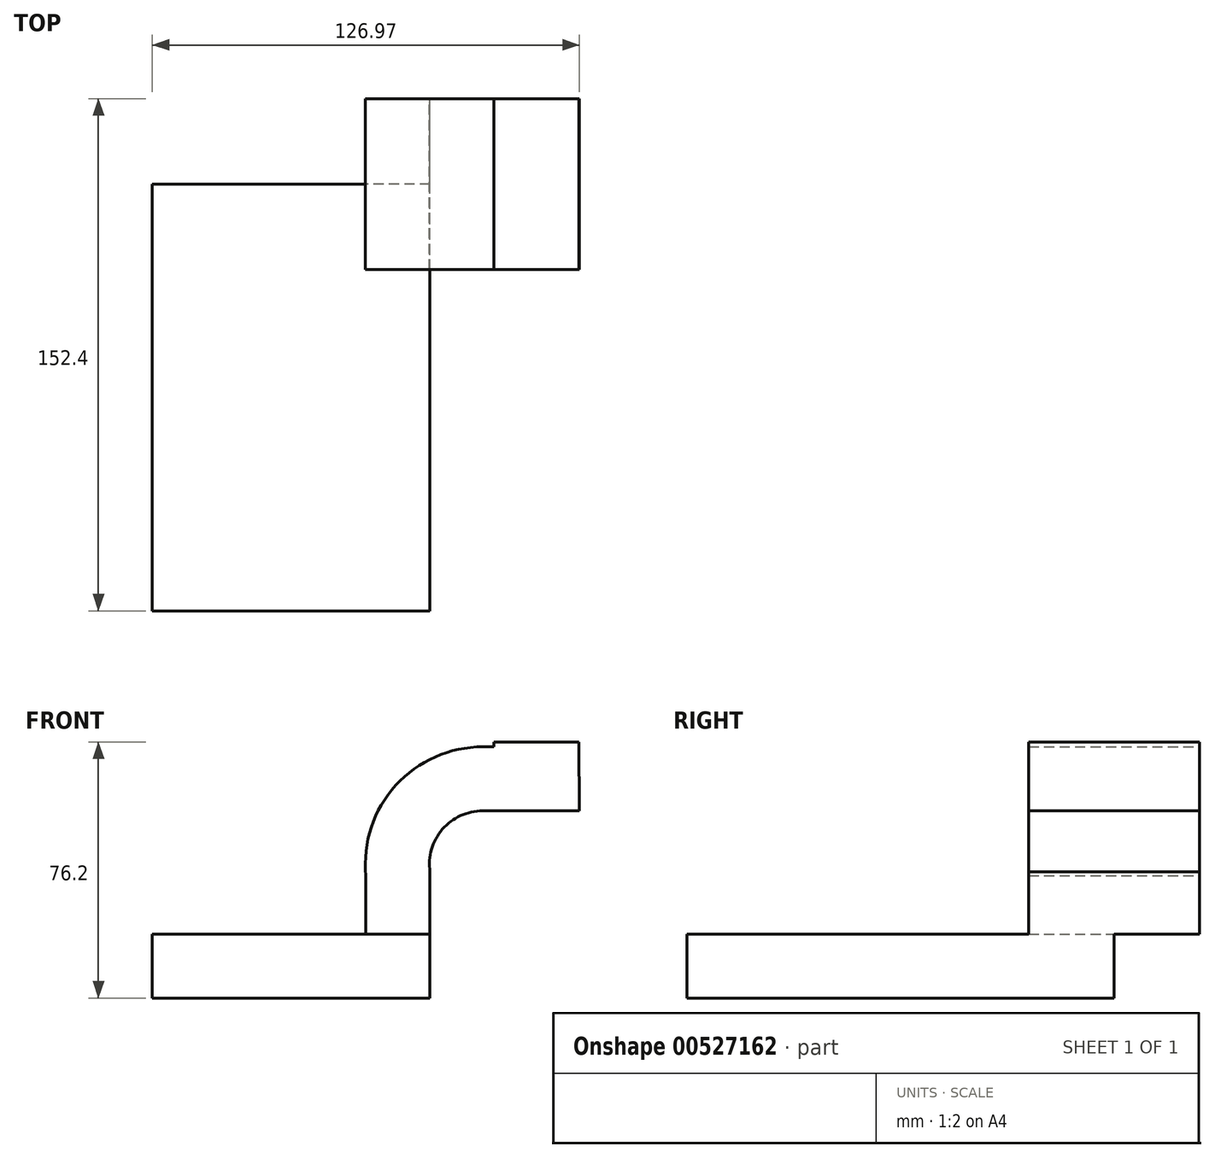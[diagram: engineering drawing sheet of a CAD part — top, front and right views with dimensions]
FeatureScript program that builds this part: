
annotation { "Feature Type Name" : "Feature", "Feature Type Description" : "" }
export const myFeature = defineFeature(function(context is Context, id is Id, definition is map)
    precondition{}
    {
        {
            var Q0;
            Q0=qCreatedBy(makeId("Front.planeOp"),FACE);
            var sketch = newSketch(context, id + "F0", { "sketchPlane" : qUnion([Q0])});
            skLineSegment(sketch, "E0.bottom", {"start": v(41.27, 9.53) * mm, "end": v(-41.28, 9.53) * mm});
            skLineSegment(sketch, "E0.top", {"start": v(41.28, -9.52) * mm, "end": v(-41.27, -9.52) * mm});
            skLineSegment(sketch, "E0.left", {"start": v(41.27, 9.53) * mm, "end": v(41.28, -9.52) * mm});
            skLineSegment(sketch, "E0.right", {"start": v(-41.28, 9.53) * mm, "end": v(-41.27, -9.52) * mm});
            skPoint(sketch, "E0.middle", {"position": v(0, 0) * mm});
            skLineSegment(sketch, "E1.bottom", {"start": v(60.33, 66.68) * mm, "end": v(111.13, 66.68) * mm});
            skLineSegment(sketch, "E1.top", {"start": v(60.33, 38.1) * mm, "end": v(111.13, 38.1) * mm});
            skLineSegment(sketch, "E1.left", {"start": v(60.33, 66.68) * mm, "end": v(60.33, 38.1) * mm});
            skLineSegment(sketch, "E1.right", {"start": v(111.13, 66.68) * mm, "end": v(111.13, 38.1) * mm});
            skPoint(sketch, "E1.middle", {"position": v(85.73, 52.39) * mm});
            skPoint(sketch, "E2.startSnap0", {"position": v(60.33, 52.39) * mm});
            skLineSegment(sketch, "E3.0", {"start": v(22.23, 9.53) * mm, "end": v(22.23, 26.86) * mm});
            skArc(sketch, "E3.1", {"start": v(56.98, 65.2) * mm, "mid": v(31.1, 53.74) * mm, "end": v(22.23, 26.86) * mm});
            skLineSegment(sketch, "E3.2", {"start": v(56.98, 65.2) * mm, "end": v(85.6, 65.2) * mm});
            skLineSegment(sketch, "E4.0", {"start": v(56.98, 46.15) * mm, "end": v(85.73, 46.15) * mm});
            skArc(sketch, "E4.1", {"start": v(56.98, 46.15) * mm, "mid": v(44.97, 40.66) * mm, "end": v(41.28, 27.98) * mm});
            skLineSegment(sketch, "E4.2", {"start": v(41.28, 9.53) * mm, "end": v(41.28, 27.98) * mm});
            skPoint(sketch, "E5", {"position": v(85.73, 38.1) * mm});
            skLineSegment(sketch, "E6", {"start": v(85.73, 38.1) * mm, "end": v(85.6, 66.68) * mm});
            skFitSpline(sketch, "E7", {"points": [v(-41.28, 9.52) * mm, v(56.98, 65.2) * mm], "startDerivative": vector(-21.96, 28.94) * mm, "endDerivative": vector(134.84, -14.37) * mm});
            skSolve(sketch);
        }
        {
            var Q0;
            Q0=makeQuery(id+"F0.imprint","IMPRINT",FACE,{"disambiguationData":[TD([[makeQuery(id+"F0.imprint","IMPRINT",EDGE,{"derivedFrom":sQuery(id+"F0.wireOp",EDGE,"E0.top")}),-1.0]])]});
            extrude(context, id + "F1", {"entities" : qUnion([Q0]), "depth" : 127 * mm, "offsetDistance" : 25.4 * mm});
        }
        {
            var Q0;
            {var subQ1=sQuery(id+"F0.wireOp",EDGE,"E3.0");Q0=makeQuery(id+"F0.imprint","IMPRINT",FACE,{"disambiguationData":[TD([[makeQuery(id+"F0.imprint","IMPRINT",EDGE,{"derivedFrom":subQ1}),-1.0]])]});}
            var Q1;
            {var subQ1=sQuery(id+"F0.wireOp",EDGE,"E1.left");var subQ5=sQuery(id+"F0.wireOp",EDGE,"E1.bottom");var subQ6=makeQuery(id+"F0.imprint","INTERSECT",VERTEX,{"derivedFrom":[subQ5,subQ1]});Q1=makeQuery(id+"F0.imprint","IMPRINT",FACE,{"disambiguationData":[TD([[makeQuery(id+"F0.imprint","IMPRINT",EDGE,{"disambiguationData":[TD([[subQ6,-1.0]])],"derivedFrom":subQ5}),-1.0]])]});}
            extrude(context, id + "F2", {"entities" : qUnion([Q0, Q1]), "operationType" : NewBodyOperationType.ADD, "endBound" : BoundingType.SYMMETRIC, "depth" : 50.8 * mm, "offsetDistance" : 25.4 * mm});
        }
    });
